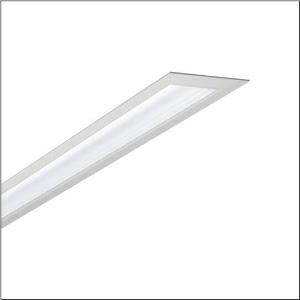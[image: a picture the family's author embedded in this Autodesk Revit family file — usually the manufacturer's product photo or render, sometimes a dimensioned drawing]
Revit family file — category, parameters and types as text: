
# Revit family: silica_r_5mx11bd1w4a_3352
name_source: partatom
category: Lighting Fixtures
units: mm (PartAtom-declared; Revit-internal decimal feet)

## family parameters
Cut with Voids When Loaded = No
Host = Face
Light Source = No
Part Type = Normal
Room Calculation Point = No
Round Connector Dimension = Use Diameter
Shared = No

## types (1)
- --- (1 x LED, 4950 lm, 29.3 W, 4000K)
    Apparent Load = 29 VA
    CIE Flux Codes = 82 97 100 100 100
    Color Rendering = 80
    Color Temperature = 4000K
    Default Elevation = 1800 mm
    Description = Silica®, office luminaire, of aluminium, light emission: direct distribution, primary light characteristic: symmetric, installation type: recessed, LED, rated luminous flux: 4.950lm, luminous efficacy: 169lm/W, light colour: 840, colour temperature: 4000K, control gear: ECG DALI, with terminal, 3+2-pole, max. 2.5mm², mains connection: 230V, AC, 50/60Hz, rated input power: 29W, luminaire housing, of aluminium, matt pure white (RAL 9010), length: 1.462mm, width: 93mm, height: 60mm, end cap, of diecast zinc, pure white (RAL 9010), protection rating (complete): IP20, insulation class (complete): insulation class I (protective earthing), certification: CE, permissible operating ambient temperature: 0..+35°C, standard: EN 50419, packaging unit: 1 piece
    Height = 0 mm  [stored 0 ft]
    Lamp = 1 x LED
    Lamp Light Flux = 4950 lm
    Lamp Power = 29.3 W
    Lamp count = 1
    Length = 1462 mm
    Luminous efficacy = 169 lm/W
    Manufacturer = Siteco
    ModVariant = No
    Model = 5MX11BD1W4A
    Mounting Place = Ceiling
    Mounting Type = Recessed
    Number of Poles = 1
    OnlyDefault = Yes
    Power Factor = 1
    Product Name = Silica®
    Product group = office luminaire | ceiling recessed
    ProductGroupID = 400
    Protection Class = Protection class I
    Protection Degree = IP 20
    RLX_Detail_Level = 1
    RLX_Emergency_Light_Flux = 0 lm
    RLX_Emergency_Type = 0
    RLX_Emergency_Type_DB = No
    RlxData = <blob elided: 24013 chars, md5=ed7b9671>
    Socket = socket
    Standby Power = 0 W
    System Light Flux = 4950 lm
    System Power = 29 W
    Type Comments = factory setting: luminous flux: 100 % | dim-lin: 254 | 163 mA
    Type Image = l_1004825.jpg
    URL = http://relux.com
    VarID = @adj_173054
    Voltage = 0 V
    Weight = 0.00 kg
    Width = 93 mm

note: [stored X ft] marks values corroborated as IEEE doubles in the binary element streams (Revit-internal decimal feet)

## geometry (parser evidence)
native form markers: Blend x4, Sweep x12
no freeform markers — native parametric forms only
